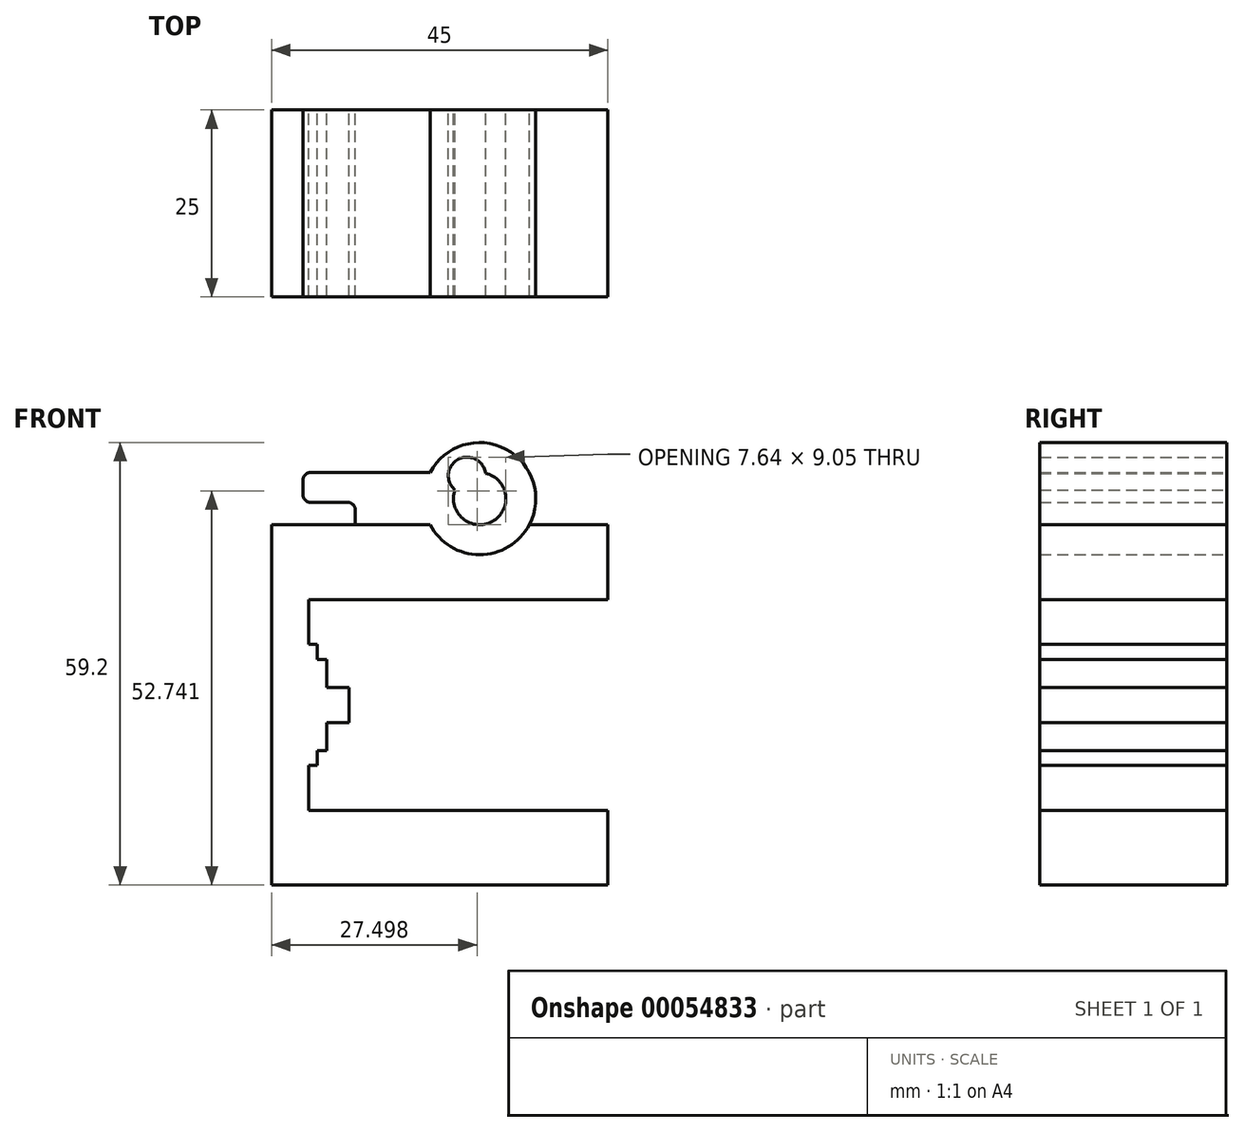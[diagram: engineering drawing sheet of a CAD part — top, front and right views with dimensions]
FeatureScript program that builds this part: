
annotation { "Feature Type Name" : "Feature", "Feature Type Description" : "" }
export const myFeature = defineFeature(function(context is Context, id is Id, definition is map)
    precondition{}
    {
        {
            var Q0;
            Q0=qCreatedBy(makeId("Front.planeOp"),FACE);
            var sketch = newSketch(context, id + "F0", { "sketchPlane" : qUnion([Q0])});
            skLineSegment(sketch, "E0", {"start": v(40, 24.1) * mm, "end": v(40, 14.1) * mm});
            skLineSegment(sketch, "E1", {"start": v(40, 14.1) * mm, "end": v(0, 14.1) * mm});
            skLineSegment(sketch, "E2", {"start": v(0, 14.1) * mm, "end": v(0, 8.1) * mm});
            skLineSegment(sketch, "E3", {"start": v(0, 8.1) * mm, "end": v(1.15, 8.1) * mm});
            skLineSegment(sketch, "E4", {"start": v(1.15, 8.1) * mm, "end": v(1.15, 6.1) * mm});
            skLineSegment(sketch, "E5", {"start": v(1.15, 6.1) * mm, "end": v(2.4, 6.1) * mm});
            skLineSegment(sketch, "E6", {"start": v(2.4, 6.1) * mm, "end": v(2.4, 2.35) * mm});
            skLineSegment(sketch, "E7", {"start": v(2.4, 2.35) * mm, "end": v(5.4, 2.35) * mm});
            skLineSegment(sketch, "E8", {"start": v(5.4, 2.35) * mm, "end": v(5.4, -2.35) * mm});
            skLineSegment(sketch, "E9", {"start": v(5.4, -2.35) * mm, "end": v(2.4, -2.35) * mm});
            skLineSegment(sketch, "E10", {"start": v(2.4, -2.35) * mm, "end": v(2.4, -6.1) * mm});
            skLineSegment(sketch, "E11", {"start": v(2.4, -6.1) * mm, "end": v(1.15, -6.1) * mm});
            skLineSegment(sketch, "E12", {"start": v(1.15, -6.1) * mm, "end": v(1.15, -8.1) * mm});
            skLineSegment(sketch, "E13", {"start": v(1.15, -8.1) * mm, "end": v(0, -8.1) * mm});
            skLineSegment(sketch, "E14", {"start": v(0, -8.1) * mm, "end": v(0, -14.1) * mm});
            skLineSegment(sketch, "E15", {"start": v(0, 14.1) * mm, "end": v(0, -14.1) * mm, "construction": true});
            skLineSegment(sketch, "E16", {"start": v(58.91, 0) * mm, "end": v(-58.91, 0) * mm, "construction": true});
            skLineSegment(sketch, "E17", {"start": v(40, 24.1) * mm, "end": v(-5, 24.1) * mm});
            skLineSegment(sketch, "E18.MirrorCS", {"start": v(40, -14.1) * mm, "end": v(0, -14.1) * mm});
            skLineSegment(sketch, "E19.MirrorCS", {"start": v(40, -24.1) * mm, "end": v(40, -14.1) * mm});
            skLineSegment(sketch, "E20.MirrorCS", {"start": v(40, -24.1) * mm, "end": v(-5, -24.1) * mm});
            skLineSegment(sketch, "E21", {"start": v(-5, 24.1) * mm, "end": v(-5, -24.1) * mm});
            skCircle(sketch, "E22", {"center": v(22.85, 27.6) * mm, "radius": 7.5 * mm});
            skCircle(sketch, "E23", {"center": v(21.16, 30.66) * mm, "radius": 2.5 * mm});
            skCircle(sketch, "E24", {"center": v(22.85, 27.6) * mm, "radius": 3.5 * mm});
            skLineSegment(sketch, "E25", {"start": v(16.22, 24.1) * mm, "end": v(6.22, 24.1) * mm});
            skLineSegment(sketch, "E26", {"start": v(6.22, 24.1) * mm, "end": v(6.22, 27.1) * mm});
            skLineSegment(sketch, "E27", {"start": v(6.22, 27.1) * mm, "end": v(-0.78, 27.1) * mm});
            skLineSegment(sketch, "E28", {"start": v(-0.78, 27.1) * mm, "end": v(-0.78, 31.1) * mm});
            skLineSegment(sketch, "E29", {"start": v(-0.78, 31.1) * mm, "end": v(16.22, 31.1) * mm});
            skSolve(sketch);
        }
        {
            var Q0;
            {var subQ0=sQuery(id+"F0.wireOp",EDGE,"2e698d56-66e1-4068-b6da-b7dfd98970b3");var subQ5=sQuery(id+"F0.wireOp",EDGE,"af75bf1d-3890-42f3-9b20-a53d7ffd6f08");var subQ6=makeQuery(id+"F0.imprint","INTERSECT",VERTEX,{"disambiguationData":[OD(1.0)],"derivedFrom":[subQ0,subQ5]});Q0=makeQuery(id+"F0.imprint","IMPRINT",FACE,{"disambiguationData":[TD([[makeQuery(id+"F0.imprint","IMPRINT",EDGE,{"disambiguationData":[TD([[subQ6,-1.0]])],"derivedFrom":subQ5}),-1.0]])]});}
            var Q1;
            {var subQ0=sQuery(id+"F0.wireOp",EDGE,"2e698d56-66e1-4068-b6da-b7dfd98970b3");var subQ3=sQuery(id+"F0.wireOp",EDGE,"f5eaa771-5305-47c8-8691-45dbc096ff13");var subQ5=makeQuery(id+"F0.imprint","INTERSECT",VERTEX,{"disambiguationData":[OD(0.0)],"derivedFrom":[subQ0,subQ3]});Q1=makeQuery(id+"F0.imprint","IMPRINT",FACE,{"disambiguationData":[TD([[makeQuery(id+"F0.imprint","IMPRINT",EDGE,{"disambiguationData":[TD([[subQ5,1.0]])],"derivedFrom":subQ3}),-1.0]])]});}
            var Q2;
            {var subQ1=sQuery(id+"F0.wireOp",EDGE,"E1");Q2=makeQuery(id+"F0.imprint","IMPRINT",FACE,{"disambiguationData":[TD([[makeQuery(id+"F0.imprint","IMPRINT",EDGE,{"derivedFrom":subQ1}),-1.0]])]});}
            extrude(context, id + "F1", {"entities" : qUnion([Q0, Q1, Q2]), "depth" : 25 * mm});
        }
        {
            var Q0;
            {var subQ1=sQuery(id+"F0.wireOp",EDGE,"054726d1-02c6-432d-a0a1-d2482c78fa46");Q0=makeQuery(id+"F0.imprint","IMPRINT",FACE,{"disambiguationData":[TD([[makeQuery(id+"F0.imprint","IMPRINT",EDGE,{"derivedFrom":subQ1}),1.0]])]});}
            var Q1;
            {var subQ0=sQuery(id+"F0.wireOp",EDGE,"f5eaa771-5305-47c8-8691-45dbc096ff13");var subQ6=sQuery(id+"F0.wireOp",EDGE,"af75bf1d-3890-42f3-9b20-a53d7ffd6f08");var subQ9=makeQuery(id+"F0.imprint","INTERSECT",VERTEX,{"disambiguationData":[OD(0.0)],"derivedFrom":[subQ6,subQ0]});Q1=makeQuery(id+"F0.imprint","IMPRINT",FACE,{"disambiguationData":[TD([[makeQuery(id+"F0.imprint","IMPRINT",EDGE,{"disambiguationData":[TD([[subQ9,-1.0]])],"derivedFrom":subQ6}),-1.0]])]});}
            var Q2;
            {var subQ4=sQuery(id+"F0.wireOp",EDGE,"af75bf1d-3890-42f3-9b20-a53d7ffd6f08");var subQ6=sQuery(id+"F0.wireOp",EDGE,"a8f72d98-72c1-4ffe-bf13-3b3df8719895");var subQ8=makeQuery(id+"F0.imprint","INTERSECT",VERTEX,{"disambiguationData":[OD(0.0)],"derivedFrom":[subQ4,subQ6]});Q2=makeQuery(id+"F0.imprint","IMPRINT",FACE,{"disambiguationData":[TD([[makeQuery(id+"F0.imprint","IMPRINT",EDGE,{"disambiguationData":[TD([[subQ8,-1.0]])],"derivedFrom":subQ4}),-1.0]])]});}
            var Q3;
            {var subQ0=sQuery(id+"F0.wireOp",EDGE,"2e698d56-66e1-4068-b6da-b7dfd98970b3");var subQ1=sQuery(id+"F0.wireOp",EDGE,"E17");var subQ2=makeQuery(id+"F0.imprint","INTERSECT",VERTEX,{"derivedFrom":[subQ1,subQ0]});Q3=makeQuery(id+"F0.imprint","IMPRINT",FACE,{"disambiguationData":[TD([[makeQuery(id+"F0.imprint","IMPRINT",EDGE,{"disambiguationData":[TD([[subQ2,-1.0]])],"derivedFrom":subQ1}),1.0]])]});}
            var Q4;
            {var subQ5=sQuery(id+"F0.wireOp",EDGE,"2e698d56-66e1-4068-b6da-b7dfd98970b3");var subQ6=sQuery(id+"F0.wireOp",EDGE,"E17");var subQ7=makeQuery(id+"F0.imprint","INTERSECT",VERTEX,{"derivedFrom":[subQ6,subQ5]});Q4=makeQuery(id+"F0.imprint","IMPRINT",FACE,{"disambiguationData":[TD([[makeQuery(id+"F0.imprint","IMPRINT",EDGE,{"disambiguationData":[TD([[subQ7,-1.0]])],"derivedFrom":subQ6}),-1.0]])]});}
            var Q5;
            {var subQ0=sQuery(id+"F0.wireOp",EDGE,"a8f72d98-72c1-4ffe-bf13-3b3df8719895");var subQ1=sQuery(id+"F0.wireOp",EDGE,"23bc6364-f650-4d89-baa6-ae6e2e4134fd");var subQ2=makeQuery(id+"F0.imprint","INTERSECT",VERTEX,{"disambiguationData":[OD(0.0)],"derivedFrom":[subQ1,subQ0]});Q5=makeQuery(id+"F0.imprint","IMPRINT",FACE,{"disambiguationData":[TD([[makeQuery(id+"F0.imprint","IMPRINT",EDGE,{"disambiguationData":[TD([[subQ2,-1.0]])],"derivedFrom":subQ1}),1.0]])]});}
            var Q6;
            {var subQ0=sQuery(id+"F0.wireOp",EDGE,"23bc6364-f650-4d89-baa6-ae6e2e4134fd");var subQ1=sQuery(id+"F0.wireOp",EDGE,"2e698d56-66e1-4068-b6da-b7dfd98970b3");var subQ2=makeQuery(id+"F0.imprint","INTERSECT",VERTEX,{"disambiguationData":[OD(0.0)],"derivedFrom":[subQ1,subQ0]});Q6=makeQuery(id+"F0.imprint","IMPRINT",FACE,{"disambiguationData":[TD([[makeQuery(id+"F0.imprint","IMPRINT",EDGE,{"disambiguationData":[TD([[subQ2,-1.0]])],"derivedFrom":subQ1}),-1.0]])]});}
            var Q7;
            {var subQ0=sQuery(id+"F0.wireOp",EDGE,"a8f72d98-72c1-4ffe-bf13-3b3df8719895");var subQ1=sQuery(id+"F0.wireOp",EDGE,"af75bf1d-3890-42f3-9b20-a53d7ffd6f08");var subQ2=makeQuery(id+"F0.imprint","INTERSECT",VERTEX,{"disambiguationData":[OD(0.0)],"derivedFrom":[subQ1,subQ0]});Q7=makeQuery(id+"F0.imprint","IMPRINT",FACE,{"disambiguationData":[TD([[makeQuery(id+"F0.imprint","IMPRINT",EDGE,{"disambiguationData":[TD([[subQ2,-1.0]])],"derivedFrom":subQ1}),1.0]])]});}
            var Q8;
            {var subQ0=sQuery(id+"F0.wireOp",EDGE,"f5eaa771-5305-47c8-8691-45dbc096ff13");var subQ1=sQuery(id+"F0.wireOp",EDGE,"23bc6364-f650-4d89-baa6-ae6e2e4134fd");var subQ2=makeQuery(id+"F0.imprint","INTERSECT",VERTEX,{"disambiguationData":[OD(0.0)],"derivedFrom":[subQ1,subQ0]});Q8=makeQuery(id+"F0.imprint","IMPRINT",FACE,{"disambiguationData":[TD([[makeQuery(id+"F0.imprint","IMPRINT",EDGE,{"disambiguationData":[TD([[subQ2,-1.0]])],"derivedFrom":subQ1}),1.0]])]});}
            var Q9;
            {var subQ0=sQuery(id+"F0.wireOp",EDGE,"f5eaa771-5305-47c8-8691-45dbc096ff13");var subQ1=sQuery(id+"F0.wireOp",EDGE,"E17");var subQ2=makeQuery(id+"F0.imprint","INTERSECT",VERTEX,{"derivedFrom":[subQ1,subQ0]});Q9=makeQuery(id+"F0.imprint","IMPRINT",FACE,{"disambiguationData":[TD([[makeQuery(id+"F0.imprint","IMPRINT",EDGE,{"disambiguationData":[TD([[subQ2,-1.0]])],"derivedFrom":subQ1}),1.0]])]});}
            var Q10;
            {var subQ4=sQuery(id+"F0.wireOp",EDGE,"f5eaa771-5305-47c8-8691-45dbc096ff13");var subQ5=sQuery(id+"F0.wireOp",EDGE,"af75bf1d-3890-42f3-9b20-a53d7ffd6f08");var subQ6=makeQuery(id+"F0.imprint","INTERSECT",VERTEX,{"disambiguationData":[OD(0.0)],"derivedFrom":[subQ5,subQ4]});Q10=makeQuery(id+"F0.imprint","IMPRINT",FACE,{"disambiguationData":[TD([[makeQuery(id+"F0.imprint","IMPRINT",EDGE,{"disambiguationData":[TD([[subQ6,-1.0]])],"derivedFrom":subQ5}),1.0]])]});}
            var Q11;
            {var subQ0=sQuery(id+"F0.wireOp",EDGE,"23bc6364-f650-4d89-baa6-ae6e2e4134fd");var subQ1=sQuery(id+"F0.wireOp",EDGE,"E17");var subQ2=makeQuery(id+"F0.imprint","INTERSECT",VERTEX,{"disambiguationData":[OD(0.0)],"derivedFrom":[subQ1,subQ0]});Q11=makeQuery(id+"F0.imprint","IMPRINT",FACE,{"disambiguationData":[TD([[makeQuery(id+"F0.imprint","IMPRINT",EDGE,{"disambiguationData":[TD([[subQ2,-1.0]])],"derivedFrom":subQ1}),-1.0]])]});}
            var Q12;
            {var subQ0=sQuery(id+"F0.wireOp",EDGE,"23bc6364-f650-4d89-baa6-ae6e2e4134fd");var subQ1=sQuery(id+"F0.wireOp",EDGE,"E17");var subQ2=makeQuery(id+"F0.imprint","INTERSECT",VERTEX,{"disambiguationData":[OD(0.0)],"derivedFrom":[subQ1,subQ0]});Q12=makeQuery(id+"F0.imprint","IMPRINT",FACE,{"disambiguationData":[TD([[makeQuery(id+"F0.imprint","IMPRINT",EDGE,{"disambiguationData":[TD([[subQ2,-1.0]])],"derivedFrom":subQ1}),1.0]])]});}
            var Q13;
            {var subQ0=sQuery(id+"F0.wireOp",EDGE,"f5eaa771-5305-47c8-8691-45dbc096ff13");var subQ1=sQuery(id+"F0.wireOp",EDGE,"E17");var subQ2=makeQuery(id+"F0.imprint","INTERSECT",VERTEX,{"derivedFrom":[subQ1,subQ0]});Q13=makeQuery(id+"F0.imprint","IMPRINT",FACE,{"disambiguationData":[TD([[makeQuery(id+"F0.imprint","IMPRINT",EDGE,{"disambiguationData":[TD([[subQ2,-1.0]])],"derivedFrom":subQ1}),-1.0]])]});}
            var Q14;
            {var subQ0=sQuery(id+"F0.wireOp",EDGE,"E24");var subQ1=sQuery(id+"F0.wireOp",EDGE,"E23");var subQ2=makeQuery(id+"F0.imprint","INTERSECT",VERTEX,{"disambiguationData":[OD(0.0)],"derivedFrom":[subQ1,subQ0]});Q14=makeQuery(id+"F0.imprint","IMPRINT",FACE,{"disambiguationData":[TD([[makeQuery(id+"F0.imprint","IMPRINT",EDGE,{"disambiguationData":[TD([[subQ2,-1.0]])],"derivedFrom":subQ1}),-1.0]])]});}
            var Q15;
            {var subQ0=sQuery(id+"F0.wireOp",EDGE,"E25");Q15=makeQuery(id+"F0.imprint","IMPRINT",FACE,{"disambiguationData":[TD([[makeQuery(id+"F0.imprint","IMPRINT",EDGE,{"derivedFrom":subQ0}),-1.0]])]});}
            extrude(context, id + "F2", {"entities" : qUnion([Q0, Q1, Q2, Q3, Q4, Q5, Q6, Q7, Q8, Q9, Q10, Q11, Q12, Q13, Q14, Q15]), "depth" : 25 * mm});
        }
        {
            var Q0;
            Q0=makeQuery(id+"F2.opExtrude","SWEPT_EDGE",EDGE,{"disambiguationData":[OSD([sQuery(id+"F0.wireOp",EDGE,"E28"),sQuery(id+"F0.wireOp",EDGE,"E29")])]});
            var Q1;
            Q1=makeQuery(id+"F2.opExtrude","SWEPT_EDGE",EDGE,{"disambiguationData":[OSD([sQuery(id+"F0.wireOp",EDGE,"E27"),sQuery(id+"F0.wireOp",EDGE,"E28")])]});
            var Q2;
            Q2=makeQuery(id+"F2.opExtrude","SWEPT_EDGE",EDGE,{"disambiguationData":[OSD([sQuery(id+"F0.wireOp",EDGE,"E26"),sQuery(id+"F0.wireOp",EDGE,"E27")])]});
            fillet(context, id + "F3", {"entities" : qUnion([Q0, Q1, Q2]), "radius" : 1 * mm, "tangentPropagation" : true, "allowEdgeOverflow" : false});
        }
    });
